# Revit family: Faucet-Lavatory-KOHLER-Composed-K-73060BR_1
name_source: partatom
category: Plumbing Fixtures
revit_build: Autodesk Revit 2017 (Build: 20160225_1515(x64)
units: mm (PartAtom-declared; Revit-internal decimal feet)

## family parameters
Cut with Voids When Loaded = No
Host = Face
OmniClass Number = 23.31.11.00
OmniClass Title = Faucets
Part Type = Normal
Room Calculation Point = No
Round Connector Dimension = Use Diameter
Shared = No

## types (4) — shared parameters
ADA Compliant = No
Assembly Code = D2010
CW Connection = Yes
Cold Water Inlet = Cold Water Inlet
Date Modified = 06/26/2020
Default Elevation = 36"
Drain Included = Yes
Flow Rate = 2 GPM
HW Connection = Yes
Handle Clearance = 3"
Height = 4 9/16"
Hot Water Inlet = Hot Water Inlet
Length = 5 15/16"
Manufacturer = KOHLER Co.
Master Format 2014 = 22 41 39
Master Format 2014 Name = Residential Faucets, Supplies, and Trim
Material = Solid Brass Construction
Pressure = 45.00 psi
Product Name = Composed
Spout Reach = 5 15/16"
URL = https://br.kohler.com
Vent Connection = No
Waste Connection = No
Waste Water Outlet = Waste Water Outlet
WaterSense Certified = No

## per-type parameters (varying)
| type | Cross Handle | Description | Dist | Finish | Lever Handle | Model | Product Page URL | Type |
| Cross Handle, CP-Polished Chrome | Yes | Widespread Lavatory Faucet-Cross Handle | 1 1/2" | Kohler-Metal-CP-Polished_Chrome | No | K-73060BR-3-CP |  | 1 |
| Lever Handle, RGD-Rose Gold | No | Widespread Lavatory Faucet-Lever Handle | 0" | Kohler-Metal-RGD-Rose_Gold | Yes | K-73060BR-4-RGD | https://br.kohler.com | 4 |
| Cross Handle, TT-Titanium Silver | Yes | Widespread Lavatory Faucet-Cross Handle | 1 1/2" | Kohler-Metal-TT-Titanium_Silver | No | K-73060BR-3-TT |  | 2 |
| Cross Handle, RGD-Rose Gold | Yes | Widespread Lavatory Faucet-Cross Handle | 1 1/2" | Kohler-Metal-RGD-Rose_Gold | No | K-73060BR-3-RGD |  | 3 |

## geometry (parser evidence)
native form markers: Sweep x8
no freeform markers — native parametric forms only
